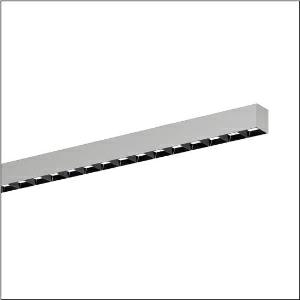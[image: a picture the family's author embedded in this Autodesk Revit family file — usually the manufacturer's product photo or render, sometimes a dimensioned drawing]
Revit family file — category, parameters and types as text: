
# Revit family: silica_r__21_51mx22tat4s_f26d
name_source: partatom
category: Lighting Fixtures
units: mm (PartAtom-declared; Revit-internal decimal feet)

## family parameters
Cut with Voids When Loaded = No
Host = Face
Light Source = No
Part Type = Normal
Room Calculation Point = No
Round Connector Dimension = Use Diameter
Shared = No

## types (1)
- --- (1 x LED, 3720 lm, 32.1 W, 6500K)
    Apparent Load = 32 VA
    CIE Flux Codes = 84 100 100 100 100
    Color Rendering = 80
    Color Temperature = 6500K
    Default Elevation = 1800 mm
    Description = Silica® 21, office luminaire, primary light control with darklight reflector, of PMMA, black, CAT 2 (L<= 3000cd/m²), light emission: direct distribution, primary light characteristic: symmetric, installation type: surface-mounted, LED, rated luminous flux: 3.720lm, luminous efficacy: 110lm/W, light colour: 8tw, colour temperature: 2700..6500K, control gear: ECG DALI, with terminal, 3+2-pole, max. 2.5mm², mains connection: 220..240V, AC, 50/60Hz, rated input power: 33.8W, luminaire housing, of aluminium, metallic grey (RAL 9006), length: 1.204mm, width: 53mm, height: 53mm, protection rating (complete): IP20, insulation class (complete): insulation class I (protective earthing), certification: CE, permissible operating ambient temperature: 0..+35°C, standard: EN 50419, packaging unit: 1 piece
    Height = 0 mm  [stored 0 ft]
    Lamp = 1 x LED
    Lamp Light Flux = 3720 lm
    Lamp Power = 32.1 W
    Lamp count = 1
    Length = 1204 mm
    Luminous efficacy = 116 lm/W
    Manufacturer = Siteco
    ModVariant = No
    Model = 51MX22TAT4S
    Mounting Place = Ceiling
    Mounting Type = Recessed
    Number of Poles = 1
    OnlyDefault = Yes
    Power Factor = 1
    Product Name = Silica® 21
    Product group = office luminaire | ceiling recessed
    ProductGroupID = 401
    Protection Class = Protection class I
    Protection Degree = IP 20
    RLX_Detail_Level = 1
    RLX_Emergency_Light_Flux = 0 lm
    RLX_Emergency_Type = 0
    RLX_Emergency_Type_DB = No
    RlxData = <blob elided: 39269 chars, md5=6b6792e0>
    Socket = socket
    Standby Power = 0 W
    System Light Flux = 3720 lm
    System Power = 32 W
    Type Comments = individual setting
    Type Image = l_1313585.jpg
    URL = http://relux.com
    VarID = @adj_089493
    Voltage = 0 V
    Weight = 0.00 kg
    Width = 53 mm

note: [stored X ft] marks values corroborated as IEEE doubles in the binary element streams (Revit-internal decimal feet)

## geometry (parser evidence)
native form markers: Blend x4, Sweep x10
no freeform markers — native parametric forms only
